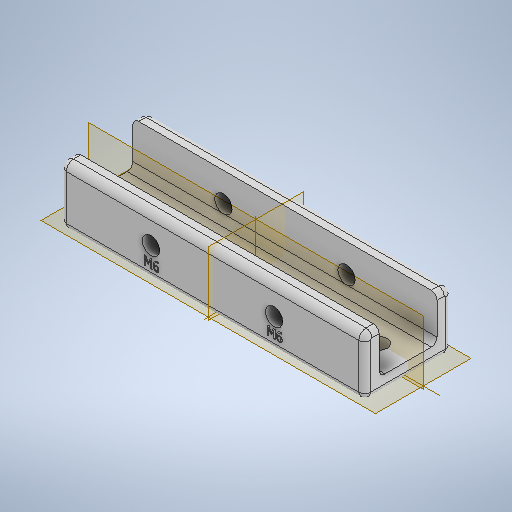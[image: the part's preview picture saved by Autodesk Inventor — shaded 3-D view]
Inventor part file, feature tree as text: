
AUTODESK INVENTOR PART (.ipt)
format: ipt  version: 2025 (Build 290162000, 162)  size: 678,912 bytes
history: native  units: mm
features: sketch x6, hole x3, emboss x2, extrude x1, fillet x1, mirror x1
ambient origin geometry x8: Origin, YZ Plane, XZ Plane, XY Plane, X Axis, Y Axis, Z Axis, Center Point
bodies: Body1 (feature_tree)
feature tree (14):
  extrude  "Extrusion2"  Depth=30.0mm
  fillet  "Fillet2"  Radius=5.0mm
  hole  "Hole4"  [1 undecoded]
  hole  "Hole5"  [1 undecoded]
  hole  "Hole6"  [1 undecoded]
  mirror  "Mirror4"
  emboss  "Emboss3"
  emboss  "Emboss4"
  sketch  "Sketch6"  dims[d35=20.0mm d36=30.0mm d37=5.0mm]
  sketch  "Sketch7"  dims[d38=2.0mm d39=2.5mm]
  sketch  "Sketch8"  dims[d40=105.0mm d41=0.0mm d42=2.0mm]
  sketch  "Sketch9"  dims[d43=6.35mm d44=6.0mm d45=4.0mm d46=2.0mm d47=90.0deg d48=8.0mm d49=20.594885mm]
  sketch  "Sketch10"  dims[d50=6.0mm d51=6.0mm d52=4.0mm d53=2.0mm d54=90.0deg d55=8.0mm d56=20.594885mm d57=42.25mm]
  sketch  "Sketch11"  dims[d58=6.0mm d59=6.0mm d60=4.0mm d61=2.0mm d62=90.0deg d63=8.0mm d64=20.594885mm d65=10.0mm d66=21.25mm d67=1.5mm d68=0.0mm d69=1.5mm d70=0.0mm]
note: 3 required parameter values undecoded (feature->parameter linkage not recoverable at this tier; creation-order binding heuristic only, values carry confidence <= 0.55)
